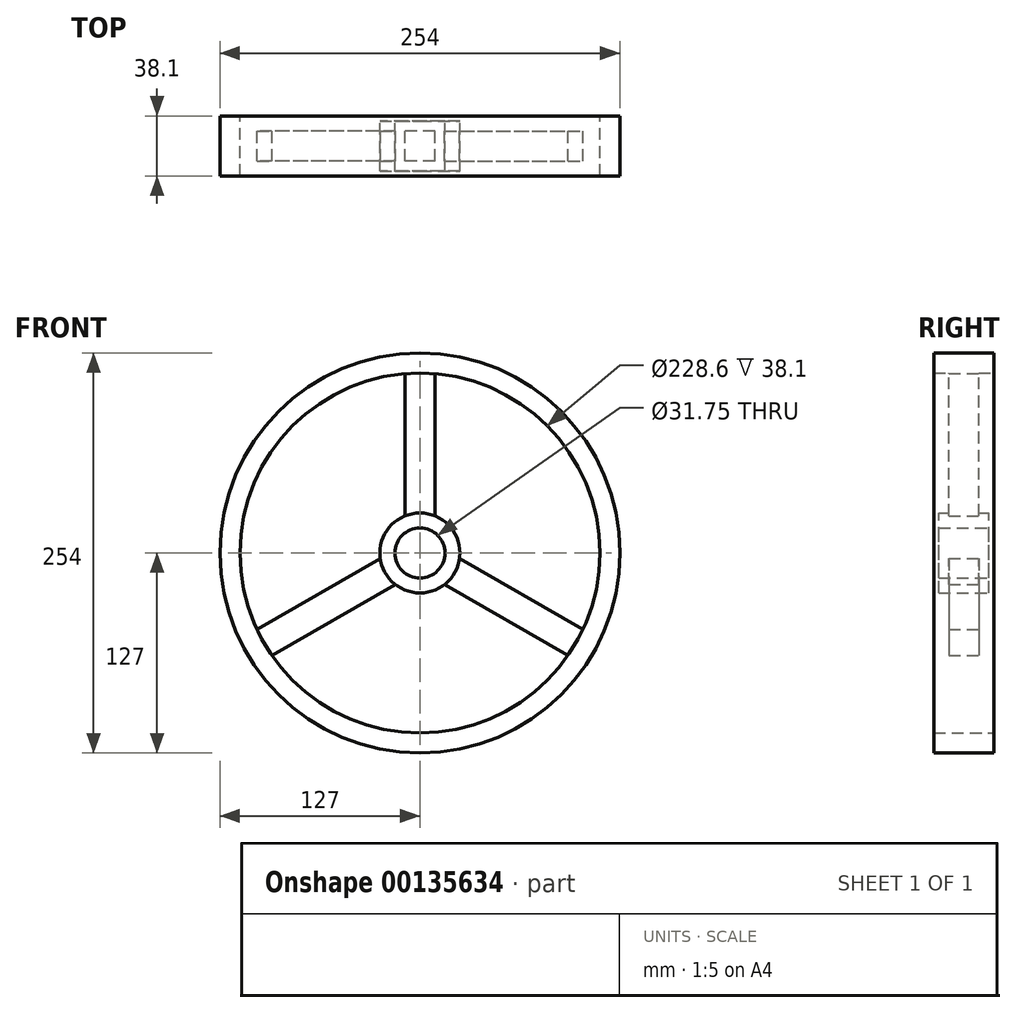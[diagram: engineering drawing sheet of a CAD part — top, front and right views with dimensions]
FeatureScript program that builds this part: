
annotation { "Feature Type Name" : "Feature", "Feature Type Description" : "" }
export const myFeature = defineFeature(function(context is Context, id is Id, definition is map)
    precondition{}
    {
        {
            var Q0;
            Q0=qCreatedBy(makeId("Front.planeOp"),FACE);
            var sketch = newSketch(context, id + "F0", { "sketchPlane" : qUnion([Q0])});
            skCircle(sketch, "E0", {"center": v(0, 0) * mm, "radius": 15.88 * mm});
            skCircle(sketch, "E1", {"center": v(0, 0) * mm, "radius": 25.4 * mm});
            skCircle(sketch, "E2", {"center": v(0, 0) * mm, "radius": 114.3 * mm});
            skCircle(sketch, "E3", {"center": v(0, 0) * mm, "radius": 127 * mm});
            skLineSegment(sketch, "E4", {"start": v(-25.15, -3.52) * mm, "end": v(-103.4, -48.7) * mm});
            skLineSegment(sketch, "E5", {"start": v(-15.63, -20.02) * mm, "end": v(-93.88, -65.2) * mm});
            skLineSegment(sketch, "E6", {"start": v(-9.53, 23.55) * mm, "end": v(-9.53, 113.9) * mm});
            skLineSegment(sketch, "E7", {"start": v(9.52, 23.55) * mm, "end": v(9.52, 113.9) * mm});
            skLineSegment(sketch, "E8", {"start": v(0, 0) * mm, "end": v(-98.99, -57.15) * mm, "construction": true});
            skLineSegment(sketch, "E9", {"start": v(0, 0) * mm, "end": v(98.99, -57.15) * mm, "construction": true});
            skLineSegment(sketch, "E10", {"start": v(25.15, -3.52) * mm, "end": v(103.4, -48.7) * mm});
            skLineSegment(sketch, "E11", {"start": v(15.63, -20.02) * mm, "end": v(93.88, -65.2) * mm});
            skSolve(sketch);
        }
        {
            var Q0;
            Q0 = qSketchRegion(id + "F0", true);
            extrude(context, id + "F1", {"entities" : qUnion([Q0]), "endBound" : BoundingType.SYMMETRIC, "depth" : 38.1 * mm});
        }
        {
            var Q0;
            {var subQ0=sQuery(id+"F0.wireOp",EDGE,"E6");Q0=makeQuery(id+"F0.imprint","IMPRINT",FACE,{"disambiguationData":[TD([[makeQuery(id+"F0.imprint","IMPRINT",EDGE,{"derivedFrom":subQ0}),-1.0]])]});}
            var Q1;
            {var subQ0=sQuery(id+"F0.wireOp",EDGE,"E4");Q1=makeQuery(id+"F0.imprint","IMPRINT",FACE,{"disambiguationData":[TD([[makeQuery(id+"F0.imprint","IMPRINT",EDGE,{"derivedFrom":subQ0}),1.0]])]});}
            var Q2;
            {var subQ0=sQuery(id+"F0.wireOp",EDGE,"E10");Q2=makeQuery(id+"F0.imprint","IMPRINT",FACE,{"disambiguationData":[TD([[makeQuery(id+"F0.imprint","IMPRINT",EDGE,{"derivedFrom":subQ0}),-1.0]])]});}
            extrude(context, id + "F2", {"entities" : qUnion([Q0, Q1, Q2]), "operationType" : NewBodyOperationType.ADD, "endBound" : BoundingType.SYMMETRIC, "depth" : 19.05 * mm});
        }
        {
            var Q0;
            Q0=makeQuery(id+"F0.imprint","IMPRINT",FACE,{"disambiguationData":[TD([[makeQuery(id+"F0.imprint","IMPRINT",EDGE,{"derivedFrom":sQuery(id+"F0.wireOp",EDGE,"E0")}),-1.0]])]});
            extrude(context, id + "F3", {"entities" : qUnion([Q0]), "operationType" : NewBodyOperationType.ADD, "endBound" : BoundingType.SYMMETRIC, "depth" : 31.75 * mm});
        }
    });
